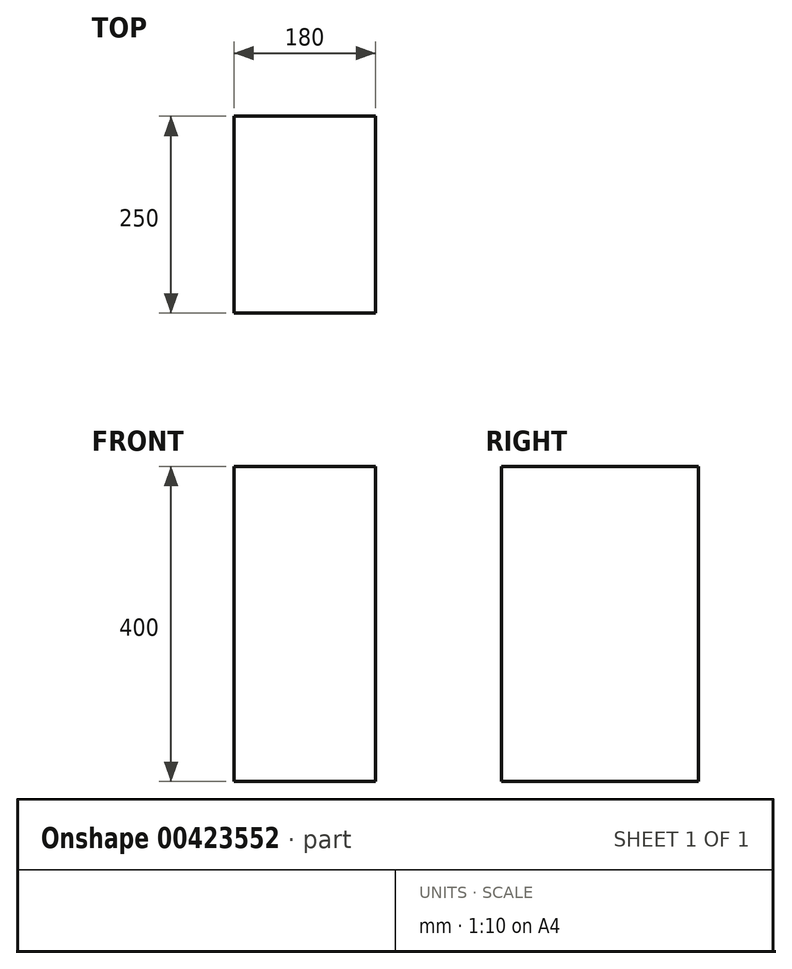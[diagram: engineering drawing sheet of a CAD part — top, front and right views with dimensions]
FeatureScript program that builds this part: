
annotation { "Feature Type Name" : "Feature", "Feature Type Description" : "" }
export const myFeature = defineFeature(function(context is Context, id is Id, definition is map)
    precondition{}
    {
        {
            var Q0;
            Q0=qCreatedBy(makeId("Top.planeOp"),FACE);
            var sketch = newSketch(context, id + "F0", { "sketchPlane" : qUnion([Q0])});
            skLineSegment(sketch, "E0.bottom", {"start": v(0, 0) * mm, "end": v(180, 0) * mm});
            skLineSegment(sketch, "E0.top", {"start": v(0, 250) * mm, "end": v(180, 250) * mm});
            skLineSegment(sketch, "E0.left", {"start": v(0, 0) * mm, "end": v(0, 250) * mm});
            skLineSegment(sketch, "E0.right", {"start": v(180, 0) * mm, "end": v(180, 250) * mm});
            skSolve(sketch);
        }
        {
            var Q0;
            Q0=makeQuery(id+"F0.imprint","IMPRINT",FACE,{"disambiguationData":[TD([[makeQuery(id+"F0.imprint","IMPRINT",EDGE,{"derivedFrom":sQuery(id+"F0.wireOp",EDGE,"E0.bottom")}),1.0]])]});
            var sketch = newSketch(context, id + "F1", { "sketchPlane" : qUnion([Q0])});
            skLineSegment(sketch, "E1.0", {"start": v(180, 0) * mm, "end": v(180, 250) * mm});
            skSolve(sketch);
        }
        {
            var Q0;
            Q0=qCreatedBy(makeId("Top.planeOp"),FACE);
            var sketch = newSketch(context, id + "F2", { "sketchPlane" : qUnion([Q0])});
            skSolve(sketch);
        }
        {
            var Q0;
            Q0 = qSketchRegion(id + "F2", true);
            var Q1;
            Q1=makeQuery(id+"F1.imprint","IMPRINT",FACE,{"disambiguationData":[TD([[makeQuery(id+"F1.imprint","IMPRINT",EDGE,{"derivedFrom":sQuery(id+"F1.wireOp",EDGE,"E1.0")}),1.0]])]});
            extrude(context, id + "F3", {"entities" : qUnion([Q0, Q1]), "depth" : 400 * mm});
        }
    });
